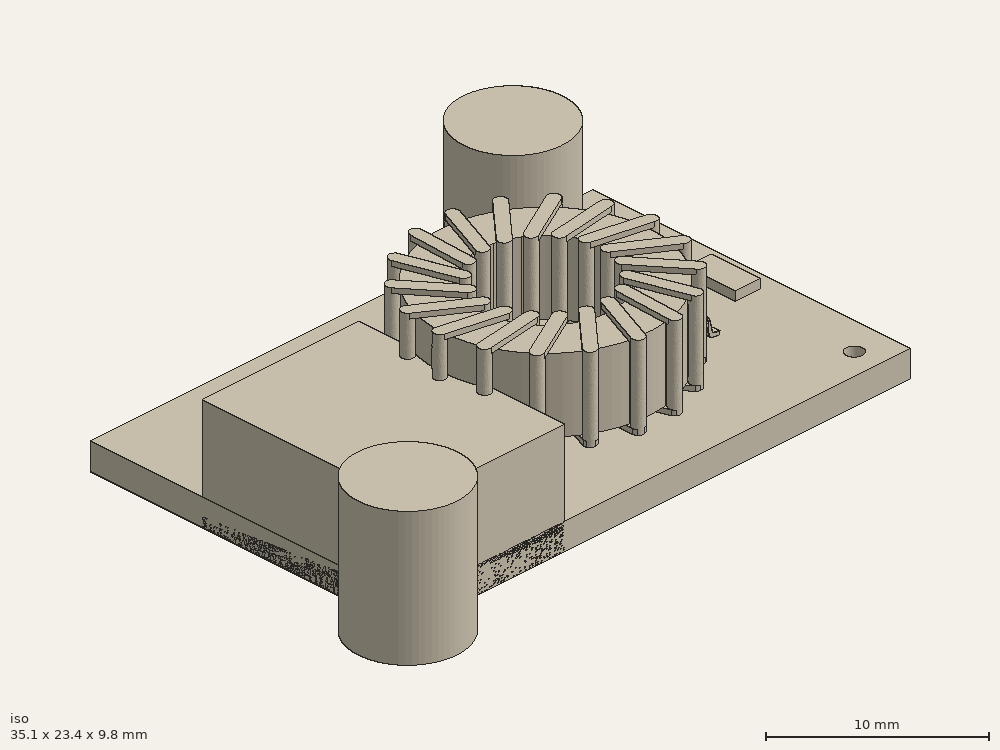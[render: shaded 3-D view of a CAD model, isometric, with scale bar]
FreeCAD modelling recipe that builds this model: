
FCSTD DOCUMENT  (FreeCAD 0.21R33771 (Git))
Label: IP6505_QC2
License: All rights reserved
LicenseURL: http://en.wikipedia.org/wiki/All_rights_reserved
objects: Sketcher::SketchObject×5, PartDesign::Pad×4, App::Part×4, PartDesign::Body×3, Part::Feature×3, Spreadsheet::Sheet×1, Part::FeaturePython×1, PartDesign::Pocket×1
note: 22 computed .brp shape members not serialized (recipe doc carries the construction recipe); baked Part::Feature solids carry a one-line shape summary decoded from their .brp

FEATURE [Spreadsheet::Sheet] Spreadsheet  label="ip6505Sp"
  cells = A2='boardLong; B2(boardLong)=32; A3='boardLarg; B3(boardLarg)=20.2; A4='boardEp; B4(boardEp)=1.6; A5='usbLong; B5(usbLong)=13.1; A6='usbLarg; B6(usbLarg)=10; A7='usbHaut; B7(usbHaut)=6.64; A8='usbPosX; B8(usbPosX)=-1.6; A9='usbPosY; B9(usbPosY)==(boardLarg - usbLong) / 2; A10='capaDiam; B10(capaDiam)=6.29; A11='capaHaut; B11(capaHaut)=8; A12='capaPosY; B12(capaPosY)=13.38; A13='capaPosZ; B13(capaPosZ)==boardEp; A14='capa1PosX; B14(capa1PosX)=16.5; A15='capa2PosX; B15(capa2PosX)=24.4
FEATURE [Sketcher::SketchObject] Sketch
  FullyConstrained = true
  MapMode = 5
  Support = -> [XY_Plane004]
  expr: Constraints[10] = <<ip6505Sp>>.boardLarg
  expr: Constraints[9] = <<ip6505Sp>>.boardLong
  sketch-geometry (4):
    g0: LineSegment StartX=0 StartY=0 StartZ=0 EndX=32 EndY=0 EndZ=0
    g1: LineSegment StartX=32 StartY=0 StartZ=0 EndX=32 EndY=20.2 EndZ=0
    g2: LineSegment StartX=32 StartY=20.2 StartZ=0 EndX=0 EndY=20.2 EndZ=0
    g3: LineSegment StartX=0 StartY=20.2 StartZ=0 EndX=0 EndY=0 EndZ=0
  constraints (11):
    c: Coincident(g0,g1)
    c: Coincident(g1,g2)
    c: Coincident(g2,g3)
    c: Coincident(g3,g0)
    c: Horizontal(g0)
    c: Horizontal(g2)
    c: Vertical(g1)
    c: Vertical(g3)
    c: Coincident(g0,g-1)
    c: DistanceX(g2,g1) = 32
    c: DistanceY(g0,g1) = 20.2
FEATURE [PartDesign::Pad] Pad
  Direction = (0,0,1)
  Length = 1.6
  Length2 = 10
  Profile = -> Sketch
  ReferenceAxis = -> Sketch [N_Axis]
  Type = 0
  expr: Length = <<ip6505Sp>>.boardEp
FEATURE [Sketcher::SketchObject] Sketch001
  FullyConstrained = true
  MapMode = 5
  Support = -> [XY_Plane005]
  expr: Constraints[10] = Spreadsheet.usbLong
  expr: Constraints[9] = <<ip6505Sp>>.usbLarg
  sketch-geometry (4):
    g0: LineSegment StartX=0 StartY=0 StartZ=0 EndX=10 EndY=0 EndZ=0
    g1: LineSegment StartX=10 StartY=0 StartZ=0 EndX=10 EndY=13.1 EndZ=0
    g2: LineSegment StartX=10 StartY=13.1 StartZ=0 EndX=0 EndY=13.1 EndZ=0
    g3: LineSegment StartX=0 StartY=13.1 StartZ=0 EndX=0 EndY=0 EndZ=0
  constraints (11):
    c: Coincident(g0,g1)
    c: Coincident(g1,g2)
    c: Coincident(g2,g3)
    c: Coincident(g3,g0)
    c: Horizontal(g0)
    c: Horizontal(g2)
    c: Vertical(g1)
    c: Vertical(g3)
    c: Coincident(g0,g-1)
    c: DistanceX(g2,g1) = 10
    c: DistanceY(g0,g1) = 13.1
FEATURE [PartDesign::Pad] Pad001
  Direction = (0,0,1)
  Length = 6.64
  Length2 = 10
  Profile = -> Sketch001
  ReferenceAxis = -> Sketch001 [N_Axis]
  Type = 0
  expr: Length = <<ip6505Sp>>.usbHaut
FEATURE [PartDesign::Body] Body001
  Group = -> [Sketch001,Pad001]
  Origin = -> Origin005
  Tip = -> Pad001
FEATURE [App::Part] Part002  label="Connector"
  Group = -> [Body001]
  Origin = -> Origin003
  Placement = pos=(-1.6,3.55,1.6) rot=(0,0,1;0rad)
  expr: .Placement.Base.x = Spreadsheet.usbPosX
  expr: .Placement.Base.y = <<ip6505Sp>>.usbPosY
  expr: .Placement.Base.z = <<ip6505Sp>>.boardEp
FEATURE [Part::Feature] Part__Feature  label="Document"
  Placement = pos=(23.74,9.06,1.56) rot=(0,0,1;1.5708rad)
  shape: bbox 6.314 x 7.023 x 3.713 mm, 402 faces, 9 solids (baked)
FEATURE [Part::Feature] Part__Feature001  label="2301-H-RC v1"
  Placement = pos=(15.81,9.84,3.38) rot=(0,0,1;0rad)
  shape: bbox 32.48 x 32.18 x 20 mm, 439 faces, 2 solids (baked)
FEATURE [Part::FeaturePython] Clone  label="2301-H-RC v002"  # Draft clone (typed FeaturePython)
  AttacherType = Attacher::AttachEngine3D
  Fuse = false
  Objects = -> [Part__Feature001]
  Placement = pos=(15.98,7.21,4.38) rot=(0,0,1;0rad)
  Scale = (0.45,0.45,0.3)
FEATURE [Sketcher::SketchObject] Sketch002
  FullyConstrained = true
  MapMode = 5
  Support = -> [XY_Plane007]
  expr: Constraints[0] = Spreadsheet.capaDiam
  sketch-geometry (1):
    g0: Circle CenterX=0 CenterY=0 CenterZ=0 NormalX=0 NormalY=0 NormalZ=1 AngleXU=0 Radius=3.145
  constraints (2):
    c: Diameter(g0) = 6.29
    c: Coincident(g0,g-1)
FEATURE [PartDesign::Pad] Pad002
  Direction = (0,0,1)
  Length = 8
  Length2 = 10
  Profile = -> Sketch002
  ReferenceAxis = -> Sketch002 [N_Axis]
  Type = 0
  expr: Length = Spreadsheet.capaHaut
FEATURE [PartDesign::Body] Body002  label="capaBdy"
  Group = -> [Sketch002,Pad002]
  Origin = -> Origin007
  Tip = -> Pad002
FEATURE [App::Part] Part003  label="capa"
  Group = -> [Body002]
  Origin = -> Origin006
  Placement = pos=(15.5,17.1,1.8) rot=(0,0,1;0rad)
FEATURE [Part::Feature] Part004  label="capa001"
  Placement = pos=(23.8,17.1,1.8) rot=(0,0,1;0rad)
  shape: bbox 6.29 x 6.29 x 8 mm, 3 faces (baked)
FEATURE [Sketcher::SketchObject] Sketch003
  FullyConstrained = true
  MapMode = 5
  Support = -> [XY_Plane004]
  sketch-geometry (2):
    g0: Circle CenterX=30 CenterY=18.939 CenterZ=0 NormalX=0 NormalY=0 NormalZ=1 AngleXU=0 Radius=0.5
    g1: Circle CenterX=30 CenterY=1.563 CenterZ=0 NormalX=0 NormalY=0 NormalZ=1 AngleXU=0 Radius=0.5
  constraints (6):
    c: DistanceY(g1,g0) = 17.376
    c: DistanceY(g-1,g1) = 1.563
    c: DistanceX(g-1,g1) = 30
    c: Equal(g1,g0)
    c: Diameter(g0) = 1
    c: Vertical(g0,g1)
FEATURE [PartDesign::Pocket] Pocket
  BaseFeature = -> Pad
  Direction = (0,0,-1)
  Length = 5
  Length2 = 5
  Profile = -> Sketch003
  ReferenceAxis = -> Sketch003 [N_Axis]
  Reversed = true
  Type = 1
FEATURE [Sketcher::SketchObject] Sketch004
  FullyConstrained = true
  MapMode = 5
  Support = -> [XY_Plane004]
  expr: Constraints[11] = Spreadsheet.boardLong - 1
  expr: Constraints[8] = Spreadsheet.boardLarg / 2 - 3.1 / 2
  sketch-geometry (4):
    g0: LineSegment StartX=29.4 StartY=11.65 StartZ=0 EndX=31 EndY=11.65 EndZ=0
    g1: LineSegment StartX=31 StartY=11.65 StartZ=0 EndX=31 EndY=8.55 EndZ=0
    g2: LineSegment StartX=31 StartY=8.55 StartZ=0 EndX=29.4 EndY=8.55 EndZ=0
    g3: LineSegment StartX=29.4 StartY=8.55 StartZ=0 EndX=29.4 EndY=11.65 EndZ=0
  constraints (12):
    c: Coincident(g0,g1)
    c: Coincident(g1,g2)
    c: Coincident(g2,g3)
    c: Coincident(g3,g0)
    c: Horizontal(g0)
    c: Horizontal(g2)
    c: Vertical(g1)
    c: Vertical(g3)
    c: DistanceY(g-1,g2) = 8.55
    c: DistanceY(g3,g3) = 3.1
    c: DistanceX(g0,g0) = 1.6
    c: DistanceX(g-1,g1) = 31
FEATURE [PartDesign::Pad] Pad003
  BaseFeature = -> Pocket
  Direction = (0,0,1)
  Length = 2.15
  Length2 = 10
  Profile = -> Sketch004
  ReferenceAxis = -> Sketch004 [N_Axis]
  Type = 0
FEATURE [PartDesign::Body] Body  label="boardBdy"
  Group = -> [Sketch,Pad,Sketch003,Pocket,Sketch004,Pad003]
  Origin = -> Origin004
  Tip = -> Pad003
FEATURE [App::Part] Part001  label="BoardPrt"
  Group = -> [Body]
  Origin = -> Origin002
FEATURE [App::Part] Part  label="IP6505Prt"
  Group = -> [Part001,Part002,Part__Feature,Part003,Part004,Clone,Spreadsheet]
  Origin = -> Origin
